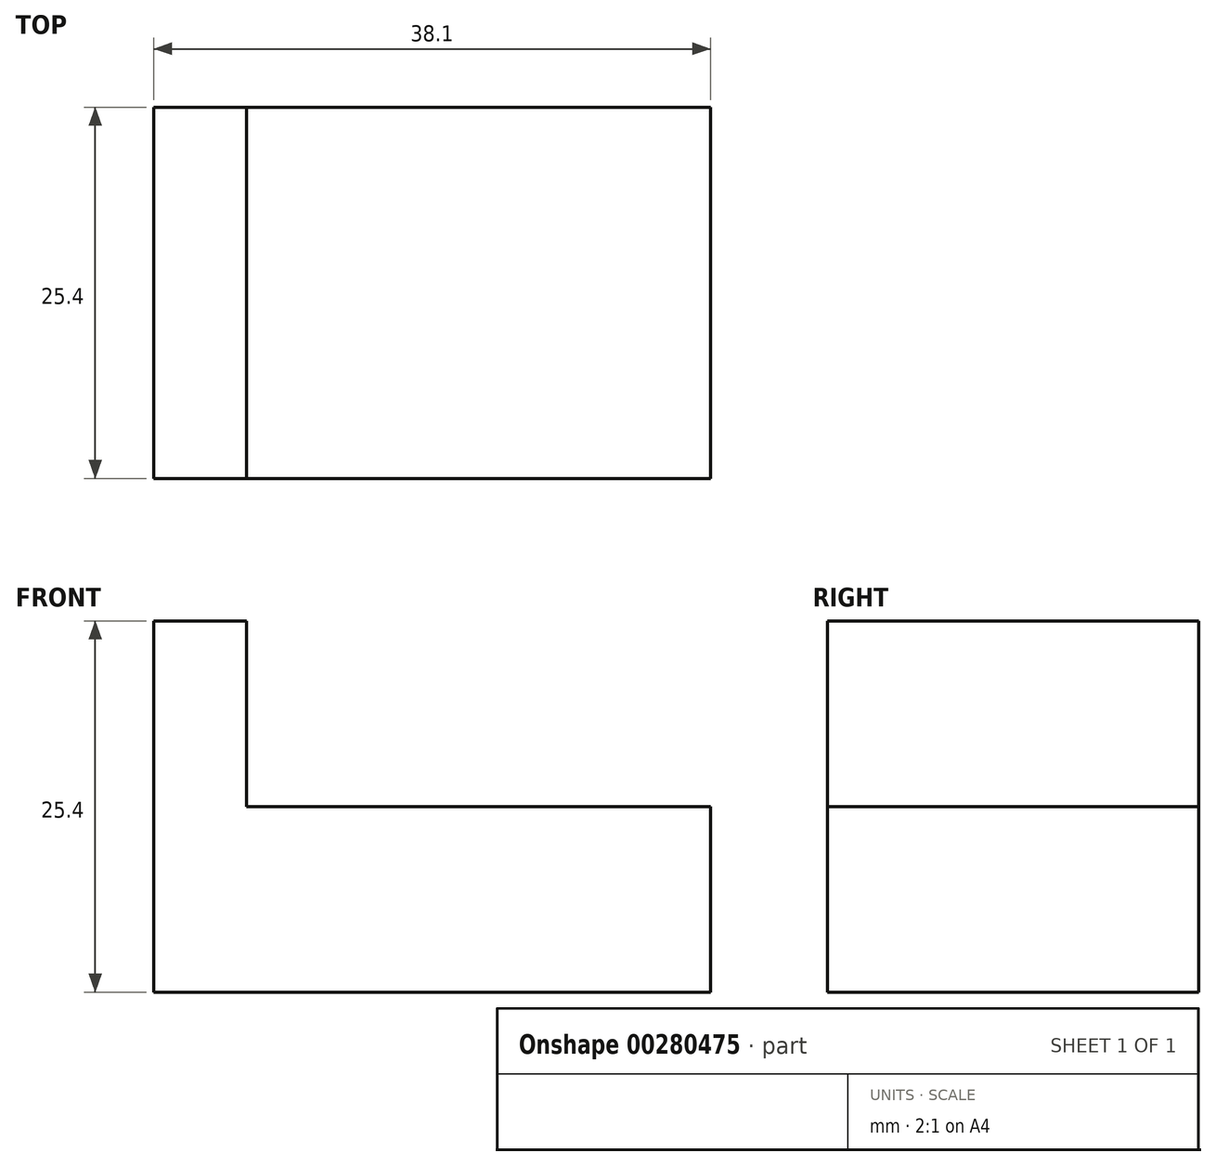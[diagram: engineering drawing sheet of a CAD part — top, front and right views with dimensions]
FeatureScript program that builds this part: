
annotation { "Feature Type Name" : "Feature", "Feature Type Description" : "" }
export const myFeature = defineFeature(function(context is Context, id is Id, definition is map)
    precondition{}
    {
        {
            var Q0;
            Q0=qCreatedBy(makeId("Front.planeOp"),FACE);
            var sketch = newSketch(context, id + "F0", { "sketchPlane" : qUnion([Q0])});
            skLineSegment(sketch, "E0", {"start": v(0, 0) * mm, "end": v(0, 25.4) * mm});
            skLineSegment(sketch, "E1", {"start": v(0, 0) * mm, "end": v(38.1, 0) * mm});
            skLineSegment(sketch, "E2", {"start": v(38.1, 0) * mm, "end": v(38.1, 12.7) * mm});
            skLineSegment(sketch, "E3", {"start": v(38.1, 12.7) * mm, "end": v(6.35, 12.7) * mm});
            skLineSegment(sketch, "E4", {"start": v(6.35, 12.7) * mm, "end": v(6.35, 25.4) * mm});
            skLineSegment(sketch, "E5", {"start": v(6.35, 25.4) * mm, "end": v(0, 25.4) * mm});
            skSolve(sketch);
        }
        {
            var Q0;
            Q0 = qSketchRegion(id + "F0", true);
            extrude(context, id + "F1", {"entities" : qUnion([Q0]), "depth" : 25.4 * mm});
        }
    });
